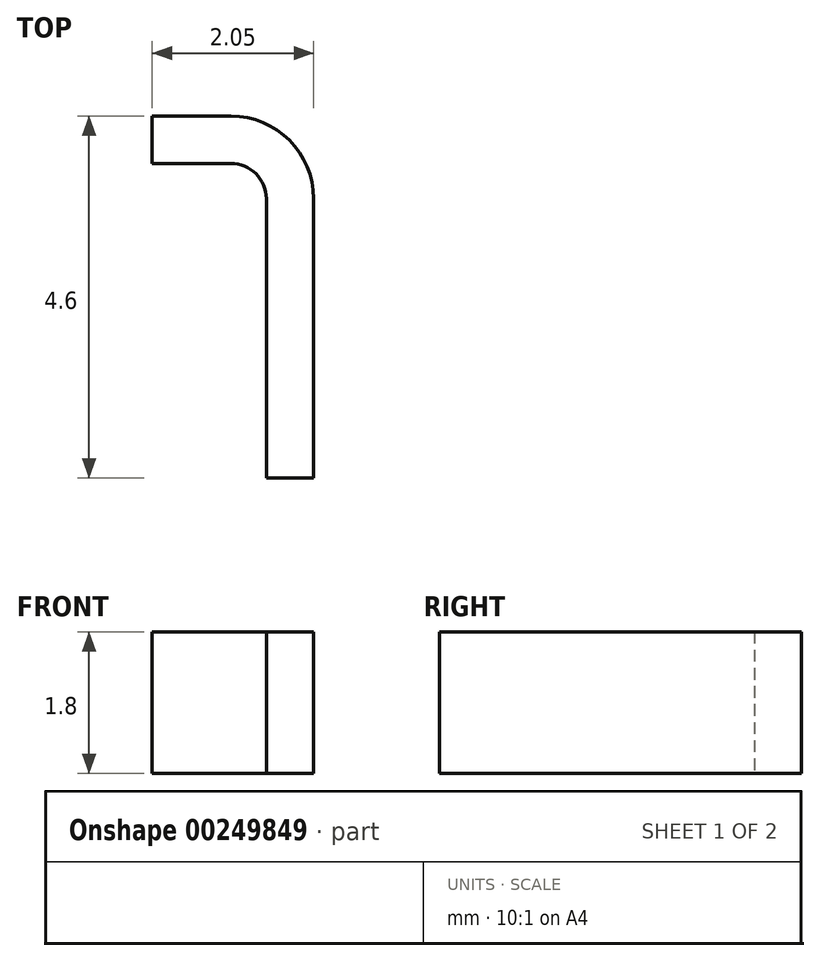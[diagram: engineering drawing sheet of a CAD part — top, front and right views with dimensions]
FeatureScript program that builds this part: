
annotation { "Feature Type Name" : "Feature", "Feature Type Description" : "" }
export const myFeature = defineFeature(function(context is Context, id is Id, definition is map)
    precondition{}
    {
        {
            var Q0;
            Q0=qCreatedBy(makeId("Top.planeOp"),FACE);
            var sketch = newSketch(context, id + "F0", { "sketchPlane" : qUnion([Q0])});
            skLineSegment(sketch, "E0", {"start": v(0, 0) * mm, "end": v(-0.6, 0) * mm});
            skLineSegment(sketch, "E1", {"start": v(-0.6, 0) * mm, "end": v(-0.6, 3.55) * mm});
            skLineSegment(sketch, "E2", {"start": v(0, 0) * mm, "end": v(0, 3.55) * mm});
            skLineSegment(sketch, "E3", {"start": v(-1.05, 4.6) * mm, "end": v(-2.05, 4.6) * mm});
            skLineSegment(sketch, "E4", {"start": v(-2.05, 4.6) * mm, "end": v(-2.05, 4) * mm});
            skLineSegment(sketch, "E5", {"start": v(-2.05, 4) * mm, "end": v(-1.05, 4) * mm});
            skArc(sketch, "E6", {"start": v(0, 3.55) * mm, "mid": v(-0.3, 4.3) * mm, "end": v(-1.05, 4.6) * mm});
            skArc(sketch, "E7", {"start": v(-0.6, 3.55) * mm, "mid": v(-0.73, 3.87) * mm, "end": v(-1.05, 4) * mm});
            skSolve(sketch);
        }
        {
            var Q0;
            Q0 = qSketchRegion(id + "F0", true);
            extrude(context, id + "F1", {"entities" : qUnion([Q0]), "depth" : 1.8 * mm});
        }
    });
